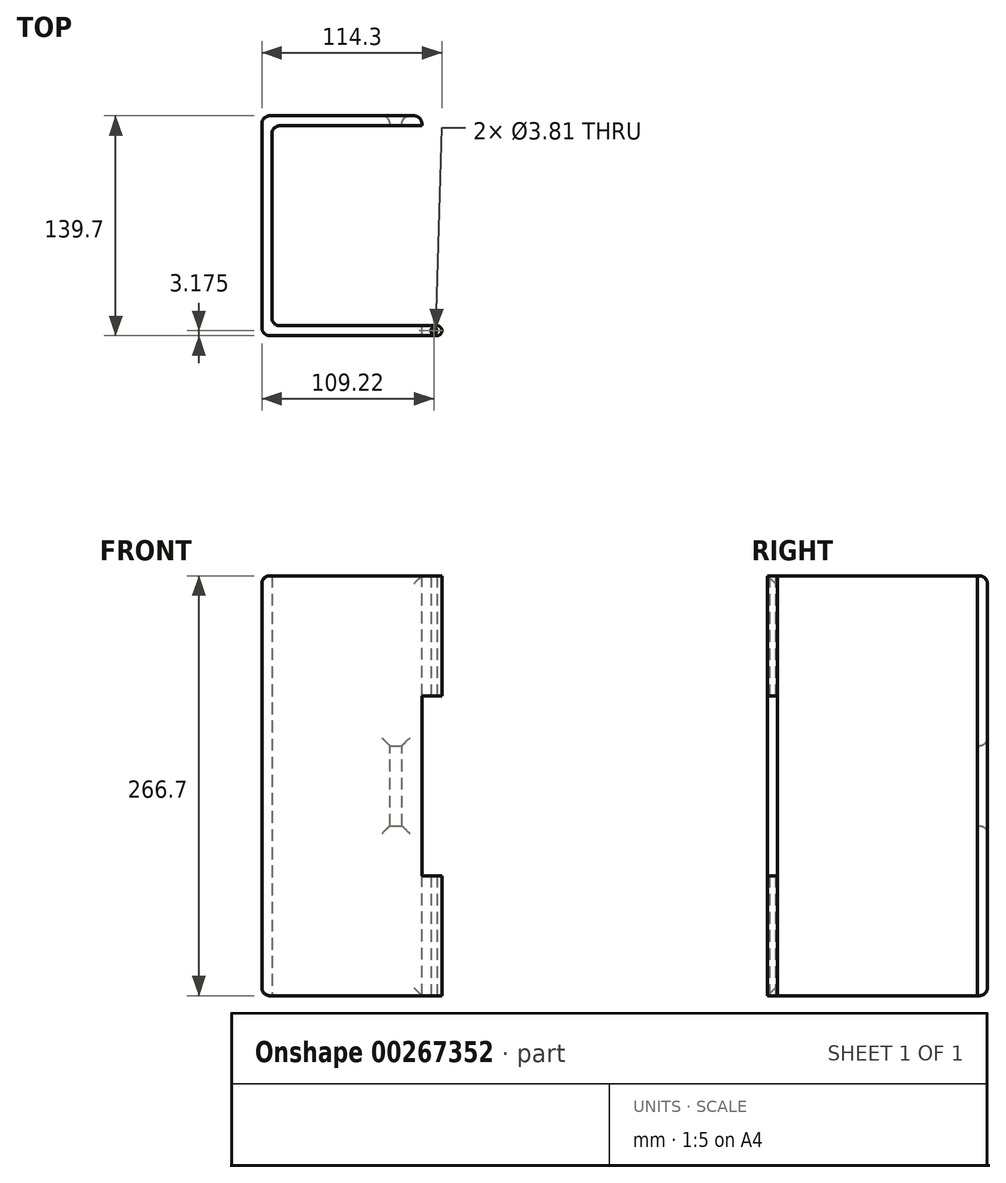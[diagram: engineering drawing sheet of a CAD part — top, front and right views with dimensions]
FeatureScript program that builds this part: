
annotation { "Feature Type Name" : "Feature", "Feature Type Description" : "" }
export const myFeature = defineFeature(function(context is Context, id is Id, definition is map)
    precondition{}
    {
        {
            var Q0;
            Q0=qCreatedBy(makeId("Front.planeOp"),FACE);
            var sketch = newSketch(context, id + "F0", { "sketchPlane" : qUnion([Q0])});
            skLineSegment(sketch, "E0.bottom", {"start": v(-127, 0) * mm, "end": v(0, 0) * mm});
            skLineSegment(sketch, "E0.top", {"start": v(-127, -266.7) * mm, "end": v(0, -266.7) * mm});
            skLineSegment(sketch, "E0.left", {"start": v(-127, 0) * mm, "end": v(-127, -266.7) * mm});
            skLineSegment(sketch, "E0.right", {"start": v(0, 0) * mm, "end": v(0, -266.7) * mm});
            skSolve(sketch);
        }
        {
            var Q0;
            Q0 = qSketchRegion(id + "F0", true);
            extrude(context, id + "F1", {"entities" : qUnion([Q0]), "depth" : 139.7 * mm});
        }
        {
            var Q0;
            Q0=makeQuery(id+"F1.opExtrude","SWEPT_FACE",FACE,{"disambiguationData":[OSD([sQuery(id+"F0.wireOp",EDGE,"E0.top")])]});
            var Q1;
            Q1=makeQuery(id+"F1.opExtrude","SWEPT_FACE",FACE,{"disambiguationData":[OSD([sQuery(id+"F0.wireOp",EDGE,"E0.bottom")])]});
            shell(context, id + "F2", {"entities" : qUnion([Q0, Q1]), "thickness" : 6.35 * mm});
        }
        {
            var Q0;
            {var subQ0=sQuery(id+"F0.wireOp",EDGE,"E0.right");Q0=makeQuery(id+"F2.opShell","OFFSET_EDGE",EDGE,{"disambiguationData":[OSD([subQ0]),TDD([makeQuery(id+"F1.opExtrude","CAP_EDGE",EDGE,{"disambiguationData":[OSD([subQ0])],"isStart":false})])]});}
            var Q1;
            {var subQ0=sQuery(id+"F0.wireOp",EDGE,"E0.left");Q1=makeQuery(id+"F2.opShell","OFFSET_EDGE",EDGE,{"disambiguationData":[OSD([subQ0]),TDD([makeQuery(id+"F1.opExtrude","CAP_EDGE",EDGE,{"disambiguationData":[OSD([subQ0])],"isStart":false})])]});}
            var Q2;
            {var subQ0=sQuery(id+"F0.wireOp",EDGE,"E0.right");Q2=makeQuery(id+"F2.opShell","OFFSET_EDGE",EDGE,{"disambiguationData":[OSD([subQ0]),TDD([makeQuery(id+"F1.opExtrude","CAP_EDGE",EDGE,{"disambiguationData":[OSD([subQ0])],"isStart":true})])]});}
            var Q3;
            {var subQ0=sQuery(id+"F0.wireOp",EDGE,"E0.left");Q3=makeQuery(id+"F2.opShell","OFFSET_EDGE",EDGE,{"disambiguationData":[OSD([subQ0]),TDD([makeQuery(id+"F1.opExtrude","CAP_EDGE",EDGE,{"disambiguationData":[OSD([subQ0])],"isStart":true})])]});}
            fillet(context, id + "F3", {"entities" : qUnion([Q0, Q1, Q2, Q3]), "radius" : 5.08 * mm, "tangentPropagation" : true, "allowEdgeOverflow" : false});
        }
        {
            var Q0;
            Q0=makeQuery(id+"F1.opExtrude","SWEPT_FACE",FACE,{"disambiguationData":[OSD([sQuery(id+"F0.wireOp",EDGE,"E0.right")])]});
            extrude(context, id + "F4", {"entities" : qUnion([Q0]), "operationType" : NewBodyOperationType.REMOVE, "oppositeDirection" : true, "depth" : 25.4 * mm});
        }
        {
            var Q0;
            Q0=makeQuery(id+"F1.opExtrude","CAP_FACE",FACE,{"disambiguationData":[OSD([sQuery(id+"F0.wireOp",EDGE,"E0.bottom"),sQuery(id+"F0.wireOp",EDGE,"E0.top"),sQuery(id+"F0.wireOp",EDGE,"E0.left"),sQuery(id+"F0.wireOp",EDGE,"E0.right")])],"isStart":true});
            var sketch = newSketch(context, id + "F5", { "sketchPlane" : qUnion([Q0])});
            skLineSegment(sketch, "E1.bottom", {"start": v(38.1, -107.95) * mm, "end": v(45.72, -107.95) * mm});
            skLineSegment(sketch, "E1.top", {"start": v(38.1, -158.75) * mm, "end": v(45.72, -158.75) * mm});
            skLineSegment(sketch, "E1.left", {"start": v(38.1, -107.95) * mm, "end": v(38.1, -158.75) * mm});
            skLineSegment(sketch, "E1.right", {"start": v(45.72, -107.95) * mm, "end": v(45.72, -158.75) * mm});
            skSolve(sketch);
        }
        {
            var Q0;
            Q0=makeQuery(id+"F5.imprint","IMPRINT",FACE,{"disambiguationData":[TD([[makeQuery(id+"F5.imprint","IMPRINT",EDGE,{"derivedFrom":sQuery(id+"F5.wireOp",EDGE,"E1.bottom")}),-1.0]])]});
            extrude(context, id + "F6", {"entities" : qUnion([Q0]), "operationType" : NewBodyOperationType.REMOVE, "oppositeDirection" : true, "depth" : 25.4 * mm});
        }
        {
            var Q0;
            Q0=makeQuery(id+"F39l0g1ojbr4QkA_1.boolean.opBoolean","MERGE",FACE,{"derivedFrom":[makeQuery(id+"F1.opExtrude","SWEPT_FACE",FACE,{"disambiguationData":[OSD([sQuery(id+"F0.wireOp",EDGE,"E0.top")])]}),makeQuery(id+"F39l0g1ojbr4QkA_1.opExtrude","SWEPT_FACE",FACE,{"disambiguationData":[OSD([sQuery(id+"FZSLRKcanwtAv7D_1.wireOp",EDGE,"GBnQNNkf-Nue4-NOAP-RjUN-CxL9uufHMIzG.bottom")])]})]});
            var sketch = newSketch(context, id + "F7", { "sketchPlane" : qUnion([Q0])});
            skCircle(sketch, "E2", {"center": v(-17.78, 136.53) * mm, "radius": 1.9 * mm});
            skSolve(sketch);
        }
        {
            var Q0;
            Q0 = qSketchRegion(id + "F7", true);
            extrude(context, id + "F8", {"entities" : qUnion([Q0]), "operationType" : NewBodyOperationType.REMOVE, "endBound" : BoundingType.THROUGH_ALL, "oppositeDirection" : true, "depth" : 25.4 * mm});
        }
        {
            var Q0;
            Q0=makeQuery(id+"F1.opExtrude","CAP_EDGE",EDGE,{"disambiguationData":[OSD([sQuery(id+"F0.wireOp",EDGE,"E0.left")])],"isStart":true});
            var Q1;
            Q1=makeQuery(id+"F1.opExtrude","SWEPT_EDGE",EDGE,{"disambiguationData":[OSD([sQuery(id+"F0.wireOp",EDGE,"E0.top"),sQuery(id+"F0.wireOp",EDGE,"E0.left")])]});
            var Q2;
            Q2=makeQuery(id+"F1.opExtrude","SWEPT_EDGE",EDGE,{"disambiguationData":[OSD([sQuery(id+"F0.wireOp",EDGE,"E0.bottom"),sQuery(id+"F0.wireOp",EDGE,"E0.left")])]});
            var Q3;
            Q3=makeQuery(id+"F1.opExtrude","CAP_EDGE",EDGE,{"disambiguationData":[OSD([sQuery(id+"F0.wireOp",EDGE,"E0.left")])],"isStart":false});
            var Q4;
            Q4=makeQuery(id+"F1.opExtrude","CAP_FACE",FACE,{"disambiguationData":[OSD([sQuery(id+"F0.wireOp",EDGE,"E0.bottom"),sQuery(id+"F0.wireOp",EDGE,"E0.top"),sQuery(id+"F0.wireOp",EDGE,"E0.left"),sQuery(id+"F0.wireOp",EDGE,"E0.right")])],"isStart":true});
            fillet(context, id + "F9", {"entities" : qUnion([Q0, Q1, Q2, Q3, Q4]), "radius" : 5.08 * mm, "tangentPropagation" : true, "allowEdgeOverflow" : false});
        }
        {
            var Q0;
            Q0=qCreatedBy(makeId("Right.planeOp"),FACE);
            cPlane(context, id + "F10", {"entities" : qUnion([Q0]), "cplaneType" : CPlaneType.OFFSET, "offset" : 25.4 * mm, "oppositeDirection" : true, "width" : 152.4 * mm, "height" : 152.4 * mm});
        }
        {
            var Q0;
            Q0=qCreatedBy(id+"F10.planeOp",FACE);
            var sketch = newSketch(context, id + "F11", { "sketchPlane" : qUnion([Q0])});
            skLineSegment(sketch, "E3.bottom", {"start": v(-139.7, 0) * mm, "end": v(-133.35, 0) * mm});
            skLineSegment(sketch, "E3.top", {"start": v(-139.7, -76.2) * mm, "end": v(-133.35, -76.2) * mm});
            skLineSegment(sketch, "E3.left", {"start": v(-139.7, 0) * mm, "end": v(-139.7, -76.2) * mm});
            skLineSegment(sketch, "E3.right", {"start": v(-133.35, 0) * mm, "end": v(-133.35, -76.2) * mm});
            skLineSegment(sketch, "E4.bottom", {"start": v(-139.7, -266.7) * mm, "end": v(-133.35, -266.7) * mm});
            skLineSegment(sketch, "E4.top", {"start": v(-139.7, -190.5) * mm, "end": v(-133.35, -190.5) * mm});
            skLineSegment(sketch, "E4.left", {"start": v(-139.7, -266.7) * mm, "end": v(-139.7, -190.5) * mm});
            skLineSegment(sketch, "E4.right", {"start": v(-133.35, -266.7) * mm, "end": v(-133.35, -190.5) * mm});
            skSolve(sketch);
        }
        {
            var Q0;
            Q0 = qSketchRegion(id + "F11", true);
            extrude(context, id + "F12", {"entities" : qUnion([Q0]), "operationType" : NewBodyOperationType.ADD, "depth" : 12.7 * mm});
        }
        {
            var Q0;
            Q0 = qSketchRegion(id + "F7", true);
            extrude(context, id + "F13", {"entities" : qUnion([Q0]), "operationType" : NewBodyOperationType.REMOVE, "endBound" : BoundingType.THROUGH_ALL, "oppositeDirection" : true, "depth" : 25.4 * mm});
        }
        {
            var Q0;
            Q0=makeQuery(id+"F12.opExtrude","CAP_EDGE",EDGE,{"disambiguationData":[OSD([sQuery(id+"F11.wireOp",EDGE,"E4.right")])],"isStart":false});
            var Q1;
            Q1=makeQuery(id+"F12.opExtrude","CAP_EDGE",EDGE,{"disambiguationData":[OSD([sQuery(id+"F11.wireOp",EDGE,"E3.right")])],"isStart":false});
            var Q2;
            Q2=makeQuery(id+"F12.opExtrude","CAP_EDGE",EDGE,{"disambiguationData":[OSD([sQuery(id+"F11.wireOp",EDGE,"E3.left")])],"isStart":false});
            var Q3;
            Q3=makeQuery(id+"F12.opExtrude","CAP_EDGE",EDGE,{"disambiguationData":[OSD([sQuery(id+"F11.wireOp",EDGE,"E4.left")])],"isStart":false});
            fillet(context, id + "F14", {"entities" : qUnion([Q0, Q1, Q2, Q3]), "radius" : 3.17 * mm, "tangentPropagation" : true, "allowEdgeOverflow" : false});
        }
    });
